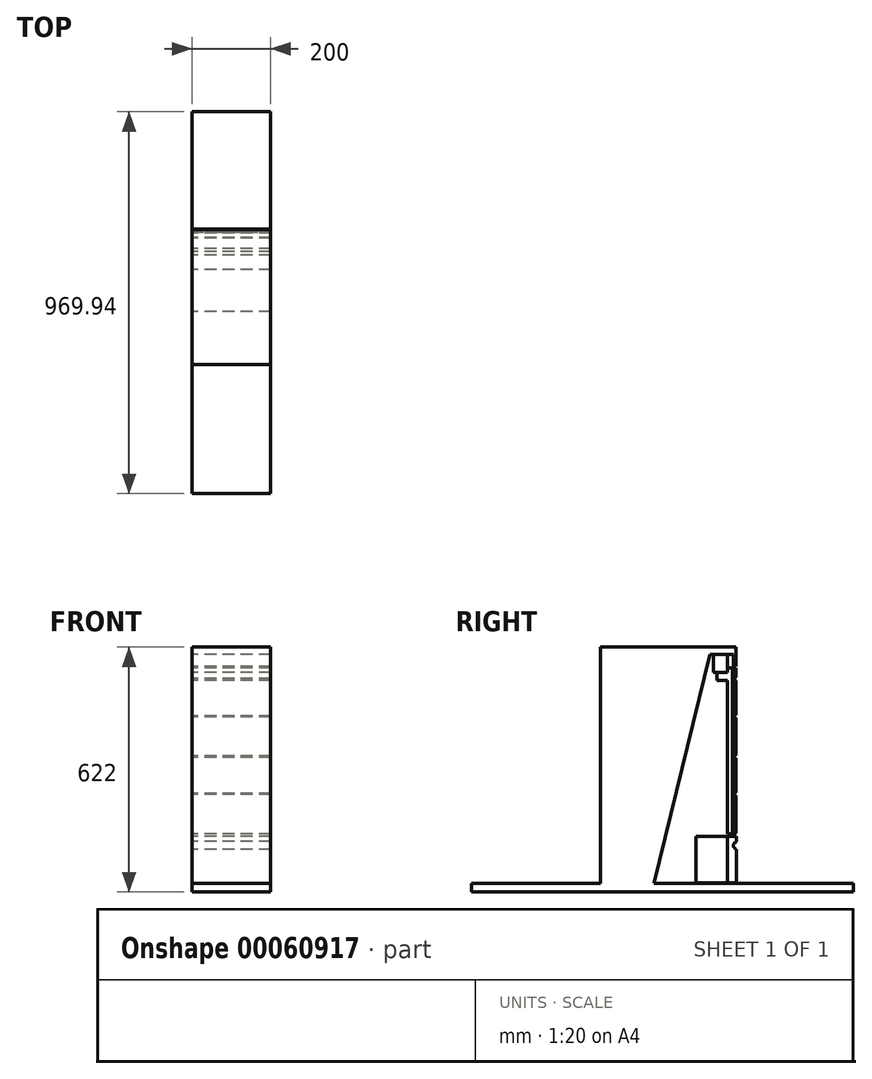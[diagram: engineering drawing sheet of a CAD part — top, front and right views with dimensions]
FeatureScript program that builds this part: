
annotation { "Feature Type Name" : "Feature", "Feature Type Description" : "" }
export const myFeature = defineFeature(function(context is Context, id is Id, definition is map)
    precondition{}
    {
        {
            var Q0;
            Q0=qCreatedBy(makeId("Right.planeOp"),FACE);
            var sketch = newSketch(context, id + "F0", { "sketchPlane" : qUnion([Q0])});
            skLineSegment(sketch, "E0.bottom", {"start": v(-755, 0) * mm, "end": v(214.94, 0) * mm});
            skLineSegment(sketch, "E0.top", {"start": v(-755, -22) * mm, "end": v(214.94, -22) * mm});
            skLineSegment(sketch, "E0.left", {"start": v(-755, 0) * mm, "end": v(-755, -22) * mm});
            skLineSegment(sketch, "E0.right", {"start": v(214.94, 0) * mm, "end": v(214.94, -22) * mm});
            skLineSegment(sketch, "E1", {"start": v(-292.21, 0) * mm, "end": v(-149.5, 581.36) * mm});
            skLineSegment(sketch, "E2", {"start": v(-149.5, 581.36) * mm, "end": v(-89.5, 581.36) * mm});
            skLineSegment(sketch, "E3", {"start": v(-83.91, 600) * mm, "end": v(-427.74, 600) * mm});
            skLineSegment(sketch, "E4", {"start": v(-427.74, 600) * mm, "end": v(-427.74, 0) * mm});
            skLineSegment(sketch, "E5", {"start": v(-427.74, 0) * mm, "end": v(-292.21, 0) * mm});
            skLineSegment(sketch, "E6.top", {"start": v(-140.9, 535.86) * mm, "end": v(-105.91, 535.86) * mm});
            skLineSegment(sketch, "E6.left", {"start": v(-140.9, 580.86) * mm, "end": v(-140.9, 535.86) * mm});
            skLineSegment(sketch, "E6.right", {"start": v(-105.91, 580.86) * mm, "end": v(-105.91, 535.86) * mm});
            skLineSegment(sketch, "E7.top", {"start": v(-185.41, 40) * mm, "end": v(-105.41, 40) * mm});
            skLineSegment(sketch, "E8.right", {"start": v(-82.62, 0.5) * mm, "end": v(-82.7, 85.58) * mm});
            skLineSegment(sketch, "E9.bottom", {"start": v(-105.41, 125) * mm, "end": v(-92.91, 125) * mm});
            skLineSegment(sketch, "E9.top", {"start": v(-105.41, 547) * mm, "end": v(-92.91, 547) * mm});
            skLineSegment(sketch, "E9.left", {"start": v(-105.41, 125) * mm, "end": v(-105.41, 547) * mm});
            skLineSegment(sketch, "E9.right", {"start": v(-92.91, 125) * mm, "end": v(-92.91, 547) * mm});
            skLineSegment(sketch, "E10.top", {"start": v(-185.41, 80) * mm, "end": v(-105.41, 80) * mm});
            skLineSegment(sketch, "E10.left", {"start": v(-185.41, 40) * mm, "end": v(-185.41, 80) * mm});
            skLineSegment(sketch, "E10.right", {"start": v(-105.41, 40) * mm, "end": v(-105.41, 80) * mm});
            skLineSegment(sketch, "E11.top", {"start": v(-185.41, 118.95) * mm, "end": v(-105.41, 118.95) * mm});
            skLineSegment(sketch, "E11.left", {"start": v(-185.41, 80) * mm, "end": v(-185.41, 118.95) * mm});
            skLineSegment(sketch, "E11.right", {"start": v(-105.41, 80) * mm, "end": v(-105.41, 118.95) * mm});
            skFitSpline(sketch, "E12", {"points": [v(-82.71, 105.57) * mm, v(-90.33, 96.15) * mm, v(-82.7, 85.58) * mm], "startDerivative": vector(-34.43, -21.9) * mm, "endDerivative": vector(34.83, -18.07) * mm});
            skLineSegment(sketch, "E13.trimOffspring", {"start": v(-82.71, 105.57) * mm, "end": v(-82.73, 118.95) * mm});
            skLineSegment(sketch, "E14.top", {"start": v(-90.91, 225) * mm, "end": v(-88.91, 225) * mm});
            skLineSegment(sketch, "E14.left", {"start": v(-90.91, 125) * mm, "end": v(-90.91, 225) * mm});
            skLineSegment(sketch, "E14.right", {"start": v(-83.91, 130) * mm, "end": v(-83.91, 220) * mm});
            skLineSegment(sketch, "E15.bottom", {"start": v(-90.91, 228) * mm, "end": v(-88.91, 228) * mm});
            skLineSegment(sketch, "E15.top", {"start": v(-90.91, 319.93) * mm, "end": v(-88.91, 319.93) * mm});
            skLineSegment(sketch, "E15.left", {"start": v(-90.91, 228) * mm, "end": v(-90.91, 319.93) * mm});
            skLineSegment(sketch, "E15.right", {"start": v(-83.91, 233) * mm, "end": v(-83.91, 314.93) * mm});
            skLineSegment(sketch, "E16.top", {"start": v(-90.91, 421.95) * mm, "end": v(-88.91, 421.95) * mm});
            skLineSegment(sketch, "E16.left", {"start": v(-90.91, 323.22) * mm, "end": v(-90.91, 421.95) * mm});
            skLineSegment(sketch, "E16.right", {"start": v(-83.91, 327.46) * mm, "end": v(-83.91, 416.95) * mm});
            skLineSegment(sketch, "E17.bottom", {"start": v(-90.91, 424.95) * mm, "end": v(-88.91, 424.95) * mm});
            skLineSegment(sketch, "E17.top", {"start": v(-90.91, 517.42) * mm, "end": v(-88.91, 517.42) * mm});
            skLineSegment(sketch, "E17.left", {"start": v(-90.91, 424.95) * mm, "end": v(-90.91, 517.42) * mm});
            skLineSegment(sketch, "E17.right", {"start": v(-83.91, 429.95) * mm, "end": v(-83.91, 512.42) * mm});
            skLineSegment(sketch, "E18", {"start": v(-90.91, 125) * mm, "end": v(-88.91, 125) * mm});
            skPoint(sketch, "E19.visualSharp", {"position": v(-83.91, 125) * mm});
            skArc(sketch, "E19.filletArc", {"start": v(-88.91, 125) * mm, "mid": v(-85.38, 126.46) * mm, "end": v(-83.91, 130) * mm});
            skPoint(sketch, "E20.visualSharp", {"position": v(-83.91, 225) * mm});
            skArc(sketch, "E20.filletArc", {"start": v(-83.91, 220) * mm, "mid": v(-85.38, 223.54) * mm, "end": v(-88.91, 225) * mm});
            skPoint(sketch, "E21.visualSharp", {"position": v(-83.91, 228) * mm});
            skArc(sketch, "E21.filletArc", {"start": v(-88.91, 228) * mm, "mid": v(-85.38, 229.46) * mm, "end": v(-83.91, 233) * mm});
            skPoint(sketch, "E22.visualSharp", {"position": v(-83.91, 319.93) * mm});
            skArc(sketch, "E22.filletArc", {"start": v(-83.91, 314.93) * mm, "mid": v(-85.38, 318.46) * mm, "end": v(-88.91, 319.93) * mm});
            skPoint(sketch, "E23.visualSharp", {"position": v(-83.91, 322.93) * mm});
            skArc(sketch, "E23.filletArc", {"start": v(-86.27, 323.22) * mm, "mid": v(-84.54, 325.04) * mm, "end": v(-83.91, 327.46) * mm});
            skPoint(sketch, "E24.visualSharp", {"position": v(-83.91, 421.95) * mm});
            skArc(sketch, "E24.filletArc", {"start": v(-83.91, 416.95) * mm, "mid": v(-85.38, 420.48) * mm, "end": v(-88.91, 421.95) * mm});
            skPoint(sketch, "E25.visualSharp", {"position": v(-83.91, 424.95) * mm});
            skArc(sketch, "E25.filletArc", {"start": v(-88.91, 424.95) * mm, "mid": v(-85.38, 426.41) * mm, "end": v(-83.91, 429.95) * mm});
            skPoint(sketch, "E26.visualSharp", {"position": v(-83.91, 517.42) * mm});
            skArc(sketch, "E26.filletArc", {"start": v(-83.91, 512.42) * mm, "mid": v(-85.38, 515.96) * mm, "end": v(-88.91, 517.42) * mm});
            skLineSegment(sketch, "E27", {"start": v(-90.91, 323.22) * mm, "end": v(-86.27, 323.22) * mm});
            skLineSegment(sketch, "E28.bottom", {"start": v(-90.91, 520.3) * mm, "end": v(-88.91, 520.3) * mm});
            skLineSegment(sketch, "E28.top", {"start": v(-90.91, 547) * mm, "end": v(-83.91, 547) * mm});
            skLineSegment(sketch, "E28.left", {"start": v(-90.91, 520.3) * mm, "end": v(-90.91, 547) * mm});
            skLineSegment(sketch, "E28.right", {"start": v(-83.91, 525.3) * mm, "end": v(-83.91, 547) * mm});
            skPoint(sketch, "E29.visualSharp", {"position": v(-83.91, 520.3) * mm});
            skArc(sketch, "E29.filletArc", {"start": v(-88.91, 520.3) * mm, "mid": v(-85.38, 521.76) * mm, "end": v(-83.91, 525.3) * mm});
            skLineSegment(sketch, "E30.bottom", {"start": v(-105.41, 535.36) * mm, "end": v(-108.41, 535.36) * mm});
            skLineSegment(sketch, "E30.top", {"start": v(-105.41, 515.36) * mm, "end": v(-108.41, 515.36) * mm});
            skLineSegment(sketch, "E30.left", {"start": v(-105.41, 535.36) * mm, "end": v(-105.41, 515.36) * mm});
            skLineSegment(sketch, "E30.right", {"start": v(-108.41, 535.36) * mm, "end": v(-108.41, 515.36) * mm});
            skLineSegment(sketch, "E31.top", {"start": v(-132.3, 515.36) * mm, "end": v(-107.3, 515.36) * mm});
            skLineSegment(sketch, "E31.right", {"start": v(-107.12, 535.36) * mm, "end": v(-107.3, 515.36) * mm});
            skLineSegment(sketch, "E32", {"start": v(-132.3, 515.36) * mm, "end": v(-132.3, 535.36) * mm});
            skLineSegment(sketch, "E33", {"start": v(-132.3, 535.36) * mm, "end": v(-107.12, 535.36) * mm});
            skLineSegment(sketch, "E34", {"start": v(-82.73, 118.95) * mm, "end": v(-104.91, 118.95) * mm});
            skLineSegment(sketch, "E35", {"start": v(-104.91, 118.95) * mm, "end": v(-104.91, 0.5) * mm});
            skLineSegment(sketch, "E36", {"start": v(-104.91, 0.5) * mm, "end": v(-82.62, 0.5) * mm});
            skLineSegment(sketch, "E37", {"start": v(-185.41, 40) * mm, "end": v(-185.41, 0.5) * mm});
            skLineSegment(sketch, "E38", {"start": v(-185.41, 0.5) * mm, "end": v(-105.41, 0.5) * mm});
            skLineSegment(sketch, "E39", {"start": v(-105.41, 0.5) * mm, "end": v(-105.41, 40) * mm});
            skLineSegment(sketch, "E40", {"start": v(-140.9, 580.86) * mm, "end": v(-105.91, 580.86) * mm});
            skLineSegment(sketch, "E41", {"start": v(-89.5, 581.36) * mm, "end": v(-89.5, 550.61) * mm});
            skLineSegment(sketch, "E42", {"start": v(-89.5, 550.61) * mm, "end": v(-83.91, 550.61) * mm});
            skLineSegment(sketch, "E43", {"start": v(-83.91, 550.61) * mm, "end": v(-83.91, 600) * mm});
            skSolve(sketch);
        }
        {
            var Q0;
            Q0 = qSketchRegion(id + "F0", true);
            extrude(context, id + "F1", {"entities" : qUnion([Q0]), "depth" : 100 * mm, "hasSecondDirection" : true, "secondDirectionOppositeDirection" : true, "secondDirectionDepth" : 100 * mm});
        }
    });
